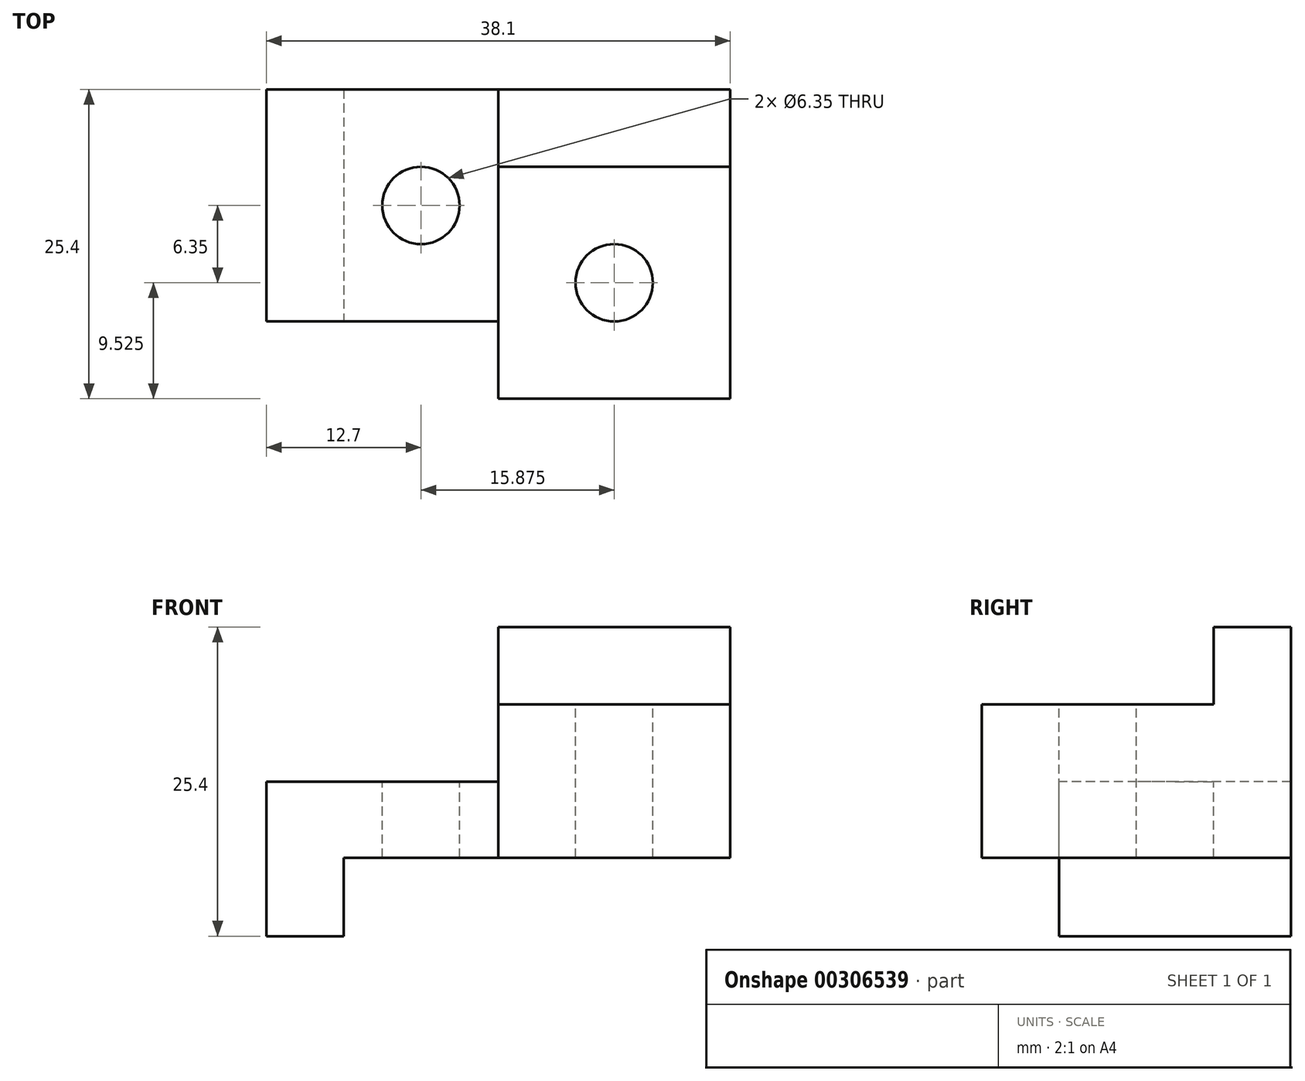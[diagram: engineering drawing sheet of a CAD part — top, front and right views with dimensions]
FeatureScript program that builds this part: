
annotation { "Feature Type Name" : "Feature", "Feature Type Description" : "" }
export const myFeature = defineFeature(function(context is Context, id is Id, definition is map)
    precondition{}
    {
        {
            var Q0;
            Q0=qCreatedBy(makeId("Front.planeOp"),FACE);
            var sketch = newSketch(context, id + "F0", { "sketchPlane" : qUnion([Q0])});
            skLineSegment(sketch, "E0", {"start": v(0, 0) * mm, "end": v(0, 25.4) * mm});
            skLineSegment(sketch, "E1", {"start": v(0, 25.4) * mm, "end": v(38.1, 25.4) * mm});
            skLineSegment(sketch, "E2", {"start": v(38.1, 25.4) * mm, "end": v(38.1, 0) * mm});
            skLineSegment(sketch, "E3", {"start": v(38.1, 0) * mm, "end": v(0, 0) * mm});
            skSolve(sketch);
        }
        {
            var Q0;
            Q0 = qSketchRegion(id + "F0", true);
            extrude(context, id + "F1", {"entities" : qUnion([Q0]), "depth" : 25.4 * mm});
        }
        {
            var Q0;
            Q0=makeQuery(id+"F1.opExtrude","CAP_FACE",FACE,{"disambiguationData":[OSD([sQuery(id+"F0.wireOp",EDGE,"E0"),sQuery(id+"F0.wireOp",EDGE,"E1"),sQuery(id+"F0.wireOp",EDGE,"E2"),sQuery(id+"F0.wireOp",EDGE,"E3")])],"isStart":false});
            var sketch = newSketch(context, id + "F2", { "sketchPlane" : qUnion([Q0])});
            skLineSegment(sketch, "E4", {"start": v(0, 25.4) * mm, "end": v(0, 12.7) * mm});
            skLineSegment(sketch, "E5", {"start": v(0, 12.7) * mm, "end": v(19.05, 12.7) * mm});
            skLineSegment(sketch, "E6", {"start": v(19.05, 12.7) * mm, "end": v(19.05, 25.4) * mm});
            skLineSegment(sketch, "E7", {"start": v(19.05, 25.4) * mm, "end": v(0, 25.4) * mm});
            skLineSegment(sketch, "E8", {"start": v(38.1, 0) * mm, "end": v(38.1, 6.45) * mm});
            skLineSegment(sketch, "E9", {"start": v(38.1, 6.45) * mm, "end": v(6.35, 6.45) * mm});
            skLineSegment(sketch, "E10", {"start": v(6.35, 6.45) * mm, "end": v(6.35, 0) * mm});
            skLineSegment(sketch, "E11", {"start": v(6.35, 0) * mm, "end": v(38.1, 0) * mm});
            skSolve(sketch);
        }
        {
            var Q0;
            Q0 = qSketchRegion(id + "F2", true);
            extrude(context, id + "F3", {"entities" : qUnion([Q0]), "operationType" : NewBodyOperationType.REMOVE, "endBound" : BoundingType.THROUGH_ALL, "oppositeDirection" : true, "depth" : 25.4 * mm});
        }
        {
            var Q0;
            Q0=makeQuery(id+"F1.opExtrude","CAP_FACE",FACE,{"disambiguationData":[OSD([sQuery(id+"F0.wireOp",EDGE,"E0"),sQuery(id+"F0.wireOp",EDGE,"E1"),sQuery(id+"F0.wireOp",EDGE,"E2"),sQuery(id+"F0.wireOp",EDGE,"E3")])],"isStart":false});
            var sketch = newSketch(context, id + "F4", { "sketchPlane" : qUnion([Q0])});
            skLineSegment(sketch, "E12", {"start": v(19.05, 25.4) * mm, "end": v(19.05, 19.05) * mm});
            skLineSegment(sketch, "E13", {"start": v(19.05, 19.05) * mm, "end": v(38.1, 19.05) * mm});
            skLineSegment(sketch, "E14", {"start": v(38.1, 19.05) * mm, "end": v(38.1, 25.4) * mm});
            skLineSegment(sketch, "E15", {"start": v(38.1, 25.4) * mm, "end": v(19.05, 25.4) * mm});
            skSolve(sketch);
        }
        {
            var Q0;
            Q0 = qSketchRegion(id + "F4", true);
            extrude(context, id + "F5", {"entities" : qUnion([Q0]), "operationType" : NewBodyOperationType.REMOVE, "oppositeDirection" : true, "depth" : 19.05 * mm});
        }
        {
            var Q0;
            Q0=makeQuery(id+"F3.boolean.opBoolean","COPY",FACE,{"derivedFrom":makeQuery(id+"F3.opExtrude","SWEPT_FACE",FACE,{"disambiguationData":[OSD([sQuery(id+"F2.wireOp",EDGE,"E5")])]})});
            var sketch = newSketch(context, id + "F6", { "sketchPlane" : qUnion([Q0])});
            skLineSegment(sketch, "E16", {"start": v(0, -25.4) * mm, "end": v(0, -19.05) * mm});
            skLineSegment(sketch, "E17", {"start": v(0, -19.05) * mm, "end": v(19.05, -19.05) * mm});
            skLineSegment(sketch, "E18", {"start": v(19.05, -19.05) * mm, "end": v(19.05, -25.4) * mm});
            skLineSegment(sketch, "E19", {"start": v(19.05, -25.4) * mm, "end": v(0, -25.4) * mm});
            skSolve(sketch);
        }
        {
            var Q0;
            Q0 = qSketchRegion(id + "F6", true);
            extrude(context, id + "F7", {"entities" : qUnion([Q0]), "operationType" : NewBodyOperationType.REMOVE, "endBound" : BoundingType.THROUGH_ALL, "oppositeDirection" : true, "depth" : 25.4 * mm});
        }
        {
            var Q0;
            Q0=makeQuery(id+"F5.boolean.opBoolean","COPY",FACE,{"derivedFrom":makeQuery(id+"F5.opExtrude","SWEPT_FACE",FACE,{"disambiguationData":[OSD([sQuery(id+"F4.wireOp",EDGE,"E13")])]})});
            var sketch = newSketch(context, id + "F8", { "sketchPlane" : qUnion([Q0])});
            skCircle(sketch, "E20", {"center": v(28.58, -15.88) * mm, "radius": 3.18 * mm});
            skCircle(sketch, "E21", {"center": v(12.7, -9.53) * mm, "radius": 3.18 * mm});
            skSolve(sketch);
        }
        {
            var Q0;
            Q0 = qSketchRegion(id + "F8", true);
            extrude(context, id + "F9", {"entities" : qUnion([Q0]), "operationType" : NewBodyOperationType.REMOVE, "endBound" : BoundingType.THROUGH_ALL, "oppositeDirection" : true, "depth" : 25.4 * mm});
        }
    });
